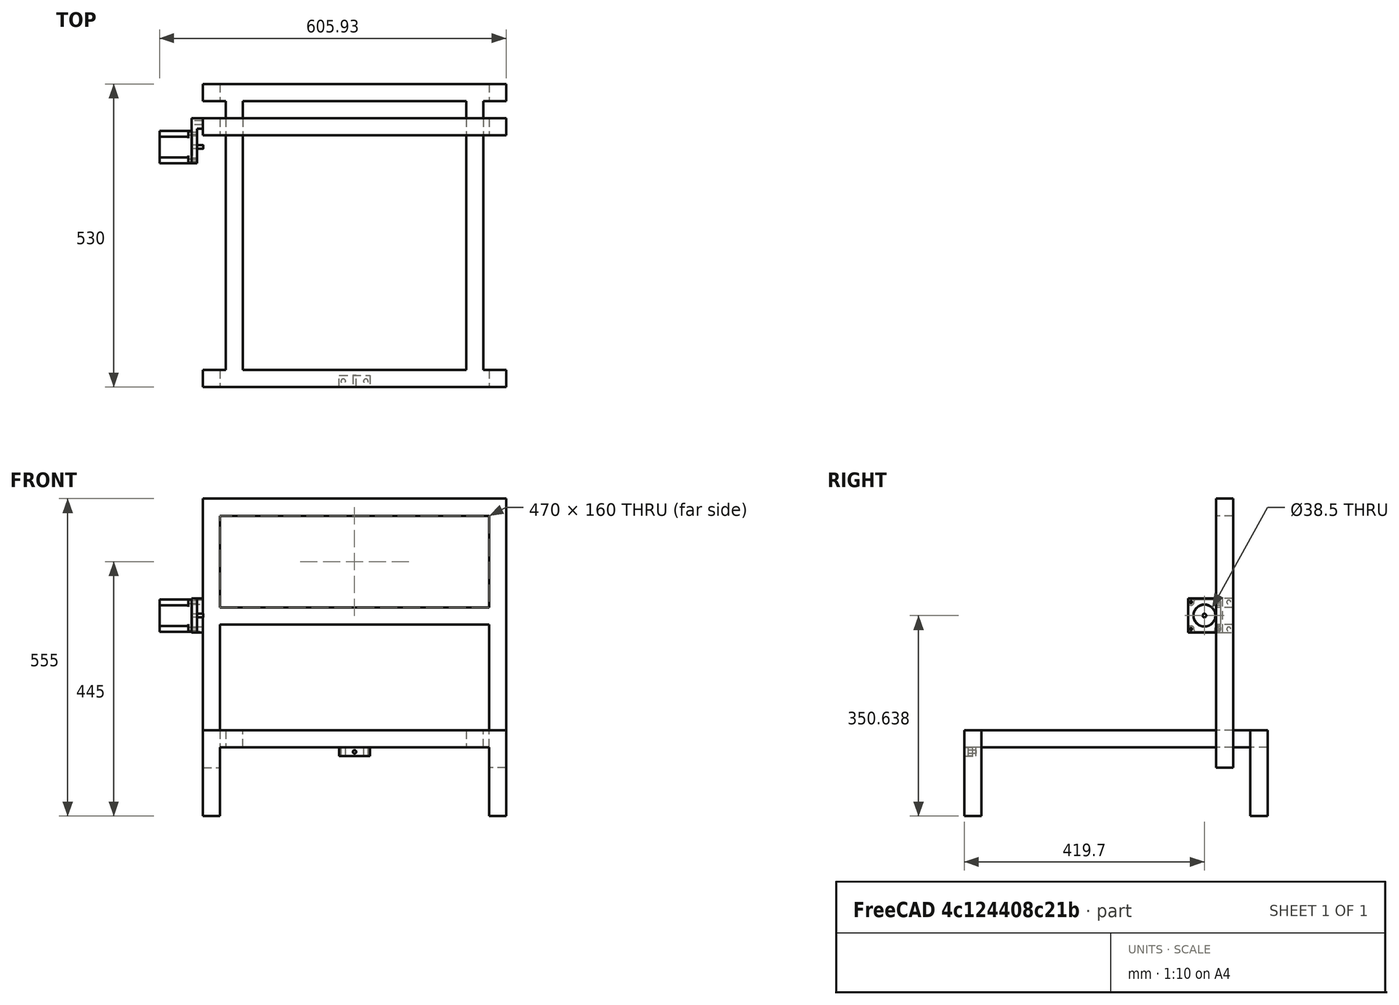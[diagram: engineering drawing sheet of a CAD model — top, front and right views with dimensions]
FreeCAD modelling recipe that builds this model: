
FCSTD DOCUMENT  (FreeCAD 0.16R6395 (Git))
Label: MaquinaCompleta
License: CreativeCommons Attribution
LicenseURL: http://creativecommons.org/licenses/by/4.0/
objects: Part::Part2DObjectPython×17, Part::Feature×7, Part::FeaturePython×4, Part::MultiFuse×1, Drawing::FeatureViewPython×1, Drawing::FeaturePage×1, App::MeasureDistance×1
note: 29 computed .brp shape members not serialized (recipe doc carries the construction recipe); baked Part::Feature solids carry a one-line shape summary decoded from their .brp

FEATURE [Part::Feature] Pad001  label="Central001"
  Placement = pos=(40,-30,120) rot=(1,0,0;1.5708rad)
  shape: bbox 30 x 470 x 30 mm, 6 faces (baked)
FEATURE [Part::Feature] Pad002  label="Frontal001"
  Placement = pos=(0,0,0) rot=(1,0,0;1.5708rad)
  shape: bbox 530 x 30 x 150 mm, 10 faces (baked)
FEATURE [Part::FeaturePython] Clone  label="Central002"  # Draft clone (typed FeaturePython)
  Objects = -> [Pad001]
  Placement = pos=(460,-30,120) rot=(1,0,0;1.5708rad)
  Scale = (1,1,1)
FEATURE [Part::FeaturePython] Clone001  label="Frontal002"  # Draft clone (typed FeaturePython)
  Objects = -> [Pad002]
  Placement = pos=(0,-500,0) rot=(1,0,0;1.5708rad)
  Scale = (1,1,1)
FEATURE [Part::Feature] Cut001001  label="SoporteMotor001"
  Placement = pos=(235,20,71.5) rot=(1,0,0;1.5708rad)
  shape: bbox 60 x 20 x 78.5 mm, 15 faces (baked)
FEATURE [Part::MultiFuse] Fusion  label="Chasis"
  Shapes = -> [Pad001,Clone001,Clone,Pad002]
FEATURE [Part::Feature] Fusion001  label="Chasis001"
  shape: bbox 530 x 530 x 150 mm, 32 faces (baked)
FEATURE [Part::Feature] Pad003  label="Puente001"
  Placement = pos=(0,-60,85) rot=(1,0,0;1.5708rad)
  shape: bbox 530 x 30 x 470 mm, 14 faces (baked)
FEATURE [Part::FeaturePython] Clone002  label="SoporteMotor002"  # Draft clone (typed FeaturePython)
  Objects = -> [Cut001001]
  Placement = pos=(-19.9309,-138.5,380.638) rot=(0,1,0;1.5708rad)
  Scale = (1,1,1)
FEATURE [Part::Part2DObjectPython] Line  # Draft 2D object (typed FeaturePython)
  ChamferSize = 0
  Closed = false
  End = (30,-60,335)
  FilletRadius = 0
  Length = 30
  MakeFace = true
  Points = (2) [(30,-60,365),(30,-60,335)]
  Start = (30,-60,365)
  Subdivisions = 0
FEATURE [Part::Part2DObjectPython] Line001  # Draft 2D object (typed FeaturePython)
  ChamferSize = 0
  Closed = false
  End = (30,-90,335)
  FilletRadius = 0
  Length = 30
  MakeFace = true
  Points = (2) [(30,-90,365),(30,-90,335)]
  Start = (30,-90,365)
  Subdivisions = 0
FEATURE [Part::Part2DObjectPython] Line002  # Draft 2D object (typed FeaturePython)
  ChamferSize = 0
  Closed = false
  End = (500,-90,335)
  FilletRadius = 0
  Length = 30
  MakeFace = true
  Points = (2) [(500,-90,365),(500,-90,335)]
  Start = (500,-90,365)
  Subdivisions = 0
FEATURE [Part::Part2DObjectPython] Line003  # Draft 2D object (typed FeaturePython)
  ChamferSize = 0
  Closed = false
  End = (500,-60,335)
  FilletRadius = 0
  Length = 30
  MakeFace = true
  Points = (2) [(500,-60,365),(500,-60,335)]
  Start = (500,-60,365)
  Subdivisions = 0
FEATURE [Part::Part2DObjectPython] Line004  # Draft 2D object (typed FeaturePython)
  ChamferSize = 0
  Closed = false
  End = (30,-90,555)
  FilletRadius = 0
  Length = 30
  MakeFace = true
  Points = (2) [(30,-90,525),(30,-90,555)]
  Start = (30,-90,525)
  Subdivisions = 0
  Support = -> Pad003
FEATURE [Part::Part2DObjectPython] Line005  # Draft 2D object (typed FeaturePython)
  ChamferSize = 0
  Closed = false
  End = (30,-60,555)
  FilletRadius = 0
  Length = 30
  MakeFace = true
  Points = (2) [(30,-60,525),(30,-60,555)]
  Start = (30,-60,525)
  Subdivisions = 0
FEATURE [Part::Part2DObjectPython] Line006  # Draft 2D object (typed FeaturePython)
  ChamferSize = 0
  Closed = false
  End = (30,-90,555)
  FilletRadius = 0
  Length = 30
  MakeFace = true
  Points = (2) [(30,-60,555),(30,-90,555)]
  Start = (30,-60,555)
  Subdivisions = 0
FEATURE [Part::Part2DObjectPython] Line007  # Draft 2D object (typed FeaturePython)
  ChamferSize = 0
  Closed = false
  End = (500,-90,555)
  FilletRadius = 0
  Length = 30
  MakeFace = true
  Points = (2) [(500,-90,525),(500,-90,555)]
  Start = (500,-90,525)
  Subdivisions = 0
FEATURE [Part::Part2DObjectPython] Line008  # Draft 2D object (typed FeaturePython)
  ChamferSize = 0
  Closed = false
  End = (500,-60,555)
  FilletRadius = 0
  Length = 30
  MakeFace = true
  Points = (2) [(500,-60,525),(500,-60,555)]
  Start = (500,-60,525)
  Subdivisions = 0
FEATURE [Part::Part2DObjectPython] Line009  # Draft 2D object (typed FeaturePython)
  ChamferSize = 0
  Closed = false
  End = (500,-60,555)
  FilletRadius = 0
  Length = 30
  MakeFace = true
  Points = (2) [(500,-90,555),(500,-60,555)]
  Start = (500,-90,555)
  Subdivisions = 0
FEATURE [Part::Part2DObjectPython] Line010  # Draft 2D object (typed FeaturePython)
  ChamferSize = 0
  Closed = false
  End = (530,-530,150)
  FilletRadius = 0
  Length = 42.4264
  MakeFace = true
  Points = (2) [(500,-530,120),(530,-530,150)]
  Start = (500,-530,120)
  Subdivisions = 0
  Support = -> Fusion001
FEATURE [Part::Part2DObjectPython] Line011  # Draft 2D object (typed FeaturePython)
  ChamferSize = 0
  Closed = false
  End = (0,-530,150)
  FilletRadius = 0
  Length = 42.4264
  MakeFace = true
  Points = (2) [(30,-530,120),(0,-530,150)]
  Start = (30,-530,120)
  Subdivisions = 0
FEATURE [Part::Part2DObjectPython] Line012  # Draft 2D object (typed FeaturePython)
  ChamferSize = 0
  Closed = false
  End = (0,0,150)
  FilletRadius = 0
  Length = 42.4264
  MakeFace = true
  Points = (2) [(30,7.99361e-14,120),(0,9.99201e-14,150)]
  Start = (30,0,120)
  Subdivisions = 0
  Support = -> Fusion001
FEATURE [Part::Part2DObjectPython] Line013  # Draft 2D object (typed FeaturePython)
  ChamferSize = 0
  Closed = false
  End = (530,0,150)
  FilletRadius = 0
  Length = 42.3741
  MakeFace = true
  Points = (2) [(500.037,7.99604e-14,120.037),(530,9.99201e-14,150)]
  Start = (500.037,0,120.037)
  Subdivisions = 0
FEATURE [Part::Part2DObjectPython] Line014  # Draft 2D object (typed FeaturePython)
  ChamferSize = 0
  Closed = false
  End = (530,-500,150)
  FilletRadius = 0
  Length = 42.4264
  MakeFace = true
  Points = (2) [(500,-500,120),(530,-500,150)]
  Start = (500,-500,120)
  Subdivisions = 0
FEATURE [Part::Part2DObjectPython] Line015  # Draft 2D object (typed FeaturePython)
  ChamferSize = 0
  Closed = false
  End = (0,-500,150)
  FilletRadius = 0
  Length = 42.4264
  MakeFace = true
  Points = (2) [(30,-500,120),(0,-500,150)]
  Start = (30,-500,120)
  Subdivisions = 0
FEATURE [Part::Part2DObjectPython] Line016  # Draft 2D object (typed FeaturePython)
  ChamferSize = 0
  Closed = false
  End = (0,-30,150)
  FilletRadius = 0
  Length = 42.4264
  MakeFace = true
  Points = (2) [(30,-30,120),(0,-30,150)]
  Start = (30,-30,120)
  Subdivisions = 0
FEATURE [Part::Feature] Fillet001001  label="Motor001"
  Placement = pos=(265,76,99.7) rot=(0,-0.707107,0.707107;3.14159rad)
  shape: bbox 56.4 x 76.6 x 56.4 mm, 37 faces (baked)
FEATURE [Part::FeaturePython] Clone003  label="Motor002"  # Draft clone (typed FeaturePython)
  Objects = -> [Fillet001001]
  Placement = pos=(-75.9309,-110.3,350.638) rot=(0.707107,0,0.707107;3.14159rad)
  Scale = (1,1,1)
FEATURE [Drawing::FeatureViewPython] ViewFusion001  # drawing view (typed FeaturePython)
  Direction = (0,0,0)
  FillStyle = 0
  FontSize = 12
  LineStyle = 0
  LineWidth = 0.35
  Rotation = 0
  Scale = 20
  Source = -> Fusion001
  ViewResult = <blob: 8730 chars omitted>
  Visible = true
  X = 200
  Y = 100
FEATURE [Drawing::FeaturePage] Page
  EditableTexts = AUTHOR NAME | CREATION DATE | SUPERVISOR NAME | CHECK DATE | SCALE | WEIGHT | NUMBER | SHEET | TITLE | SUBTITLE
  Group = -> [ViewFusion001]
FEATURE [App::MeasureDistance] Distance  label="Distance: 20,3989 mm"
  Distance = 20.3989
  P1 = (265.009,-0.600006,99.6011)
  P2 = (264.974,-0.581046,120)
FEATURE [Part::Feature] Pocket001
  Placement = pos=(265,-519.75,112.4) rot=(0,0,1;0rad)
  shape: bbox 53.5 x 20.5 x 15.2 mm, 9 faces (baked)
